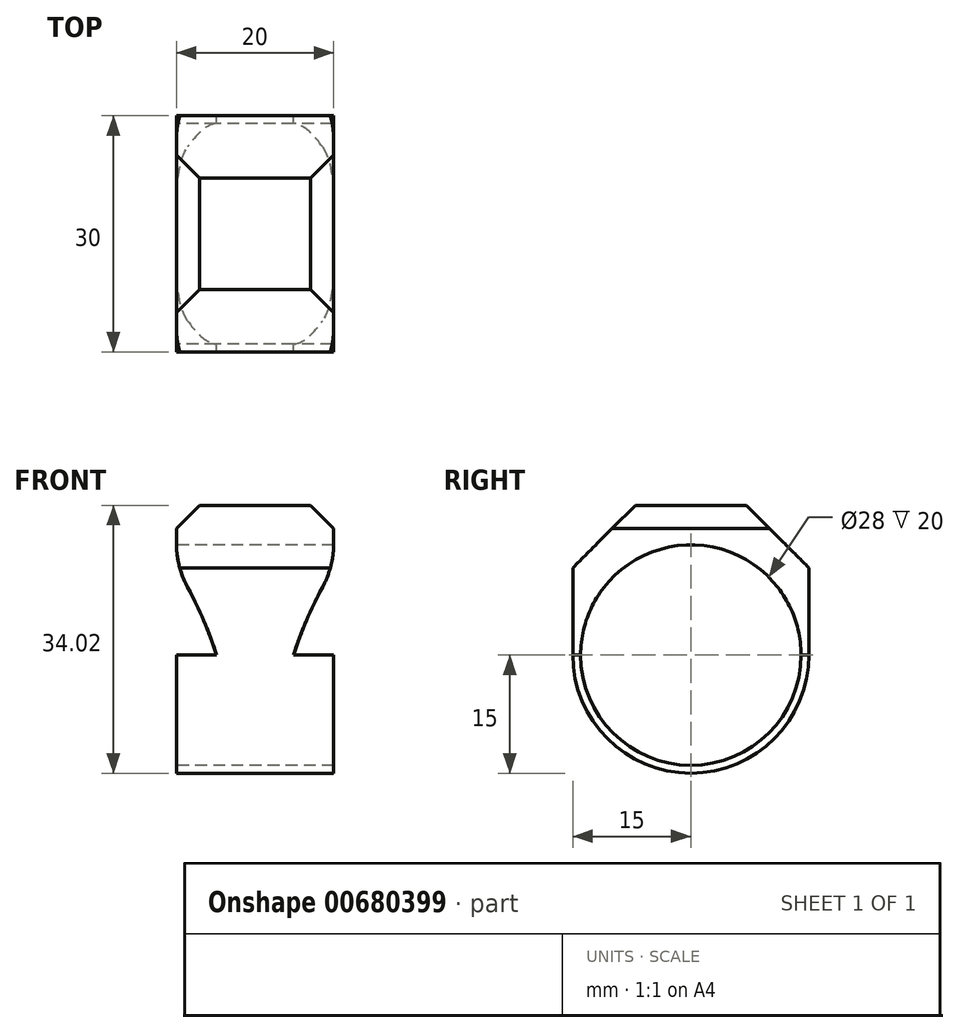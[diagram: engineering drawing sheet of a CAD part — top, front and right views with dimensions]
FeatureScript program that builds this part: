
annotation { "Feature Type Name" : "Feature", "Feature Type Description" : "" }
export const myFeature = defineFeature(function(context is Context, id is Id, definition is map)
    precondition{}
    {
        {
            var Q0;
            Q0=qCreatedBy(makeId("Right.planeOp"),FACE);
            var sketch = newSketch(context, id + "F0", { "sketchPlane" : qUnion([Q0])});
            skCircle(sketch, "E0", {"center": v(0, 0) * mm, "radius": 14 * mm});
            skArc(sketch, "E1", {"start": v(-15, 0) * mm, "mid": v(0, -15) * mm, "end": v(15, 0) * mm});
            skLineSegment(sketch, "E2", {"start": v(15, 0) * mm, "end": v(15, 21.08) * mm});
            skLineSegment(sketch, "E3", {"start": v(-15, 0) * mm, "end": v(-15, 21.08) * mm});
            skLineSegment(sketch, "E4", {"start": v(-15, 21.08) * mm, "end": v(15, 21.08) * mm});
            skSolve(sketch);
        }
        {
            var Q0;
            Q0=qSketchRegion(id+"F0",true);
            extrude(context, id + "F1", {"entities" : qUnion([Q0]), "depth" : 20 * mm, "offsetDistance" : 25 * mm});
        }
        {
            var Q0;
            Q0=makeQuery(id+"F1.opExtrude","SWEPT_EDGE",EDGE,{"disambiguationData":[OSD([sQuery(id+"F0.wireOp",EDGE,"E3"),sQuery(id+"F0.wireOp",EDGE,"E4")])]});
            var Q1;
            Q1=makeQuery(id+"F1.opExtrude","SWEPT_EDGE",EDGE,{"disambiguationData":[OSD([sQuery(id+"F0.wireOp",EDGE,"E2"),sQuery(id+"F0.wireOp",EDGE,"E4")])]});
            chamfer(context, id + "F2", {"entities" : qUnion([Q0, Q1]), "width" : 10 * mm, "tangentPropagation" : true});
        }
        {
            var Q0;
            Q0=makeQuery(id+"F1.opExtrude","SWEPT_FACE",FACE,{"disambiguationData":[OSD([sQuery(id+"F0.wireOp",EDGE,"E2")])]});
            var sketch = newSketch(context, id + "F3", { "sketchPlane" : qUnion([Q0])});
            skLineSegment(sketch, "E5", {"start": v(0, -15) * mm, "end": v(-20, -15) * mm});
            skLineSegment(sketch, "E6", {"start": v(-12.5, -15) * mm, "end": v(-7.5, -15) * mm});
            skArc(sketch, "E7", {"start": v(0, 11.08) * mm, "mid": v(-5.55, -1.44) * mm, "end": v(-7.5, -15) * mm});
            skArc(sketch, "E8", {"start": v(-12.5, -15) * mm, "mid": v(-14.45, -1.44) * mm, "end": v(-20, 11.08) * mm});
            skLineSegment(sketch, "E9", {"start": v(0, 11.08) * mm, "end": v(0, -15) * mm});
            skLineSegment(sketch, "E10", {"start": v(0, -15) * mm, "end": v(-7.5, -15) * mm});
            skLineSegment(sketch, "E11", {"start": v(-20, -15) * mm, "end": v(-20, -15) * mm});
            skLineSegment(sketch, "E12", {"start": v(-20, 11.08) * mm, "end": v(-20, -15) * mm});
            skLineSegment(sketch, "E13.trimOffspring", {"start": v(-12.5, -15) * mm, "end": v(-20, -15) * mm});
            skSolve(sketch);
        }
        {
            var Q0;
            {var subQ0=sQuery(id+"F3.wireOp",EDGE,"E9");var subQ2=sQuery(id+"F0.wireOp",EDGE,"E2");var subQ4=makeQuery(id+"F1.opExtrude","SWEPT_EDGE",EDGE,{"disambiguationData":[OSD([sQuery(id+"F0.wireOp",EDGE,"E1"),subQ2])]});var subQ6=makeQuery(id+"F3.imprint","INTERSECT",VERTEX,{"derivedFrom":[subQ4,subQ0]});Q0=makeQuery(id+"F3.imprint","IMPRINT",FACE,{"disambiguationData":[TD([[makeQuery(id+"F3.imprint","IMPRINT",EDGE,{"disambiguationData":[TD([[subQ6,1.0]])],"derivedFrom":subQ4}),1.0]])]});}
            var Q1;
            {var subQ0=sQuery(id+"F3.wireOp",EDGE,"E12");var subQ2=sQuery(id+"F0.wireOp",EDGE,"E2");var subQ4=makeQuery(id+"F1.opExtrude","SWEPT_EDGE",EDGE,{"disambiguationData":[OSD([sQuery(id+"F0.wireOp",EDGE,"E1"),subQ2])]});var subQ6=makeQuery(id+"F3.imprint","INTERSECT",VERTEX,{"derivedFrom":[subQ4,subQ0]});Q1=makeQuery(id+"F3.imprint","IMPRINT",FACE,{"disambiguationData":[TD([[makeQuery(id+"F3.imprint","IMPRINT",EDGE,{"disambiguationData":[TD([[subQ6,-1.0]])],"derivedFrom":subQ4}),1.0]])]});}
            var Q2;
            {var subQ0=sQuery(id+"F3.wireOp",EDGE,"E13.trimOffspring");Q2=makeQuery(id+"F3.imprint","IMPRINT",FACE,{"disambiguationData":[TD([[makeQuery(id+"F3.imprint","IMPRINT",EDGE,{"derivedFrom":subQ0}),-1.0]])]});}
            var Q3;
            {var subQ0=sQuery(id+"F3.wireOp",EDGE,"E10");Q3=makeQuery(id+"F3.imprint","IMPRINT",FACE,{"disambiguationData":[TD([[makeQuery(id+"F3.imprint","IMPRINT",EDGE,{"derivedFrom":subQ0}),-1.0]])]});}
            extrude(context, id + "F4", {"entities" : qUnion([Q0, Q1, Q2, Q3]), "operationType" : NewBodyOperationType.REMOVE, "oppositeDirection" : true, "depth" : 38.66 * mm, "offsetDistance" : 25 * mm});
        }
        {
            var Q0;
            {var subQ0=sQuery(id+"F0.wireOp",EDGE,"E4");var subQ1=sQuery(id+"F0.wireOp",EDGE,"E2");var subQ3=sQuery(id+"F3.wireOp",EDGE,"E8");Q0=makeQuery(id+"F4.boolean.opBoolean","COPY",EDGE,{"disambiguationData":[TD([makeQuery(id+"F1.opExtrude","SWEPT_FACE",FACE,{"disambiguationData":[OSD([subQ1])]})])],"derivedFrom":makeQuery(id+"F4.opExtrude","SWEPT_EDGE",EDGE,{"disambiguationData":[OSD([subQ1,subQ0,subQ3,sQuery(id+"F3.wireOp",EDGE,"E12")])]})});}
            var Q1;
            {var subQ0=sQuery(id+"F0.wireOp",EDGE,"E4");var subQ1=sQuery(id+"F0.wireOp",EDGE,"E3");var subQ2=sQuery(id+"F0.wireOp",EDGE,"E2");var subQ4=sQuery(id+"F3.wireOp",EDGE,"E8");Q1=makeQuery(id+"F4.boolean.opBoolean","COPY",EDGE,{"disambiguationData":[TD([makeQuery(id+"F1.opExtrude","SWEPT_FACE",FACE,{"disambiguationData":[OSD([subQ1])]})])],"derivedFrom":makeQuery(id+"F4.opExtrude","SWEPT_EDGE",EDGE,{"disambiguationData":[OSD([subQ2,subQ0,subQ4,sQuery(id+"F3.wireOp",EDGE,"E12")])]})});}
            var Q2;
            {var subQ0=sQuery(id+"F0.wireOp",EDGE,"E4");var subQ1=sQuery(id+"F0.wireOp",EDGE,"E3");var subQ2=sQuery(id+"F3.wireOp",EDGE,"E7");var subQ3=sQuery(id+"F0.wireOp",EDGE,"E2");Q2=makeQuery(id+"F4.boolean.opBoolean","COPY",EDGE,{"disambiguationData":[TD([makeQuery(id+"F1.opExtrude","SWEPT_FACE",FACE,{"disambiguationData":[OSD([subQ1])]})])],"derivedFrom":makeQuery(id+"F4.opExtrude","SWEPT_EDGE",EDGE,{"disambiguationData":[OSD([subQ3,subQ0,subQ2,sQuery(id+"F3.wireOp",EDGE,"E9")])]})});}
            var Q3;
            {var subQ0=sQuery(id+"F0.wireOp",EDGE,"E2");var subQ1=sQuery(id+"F0.wireOp",EDGE,"E4");var subQ3=sQuery(id+"F3.wireOp",EDGE,"E7");Q3=makeQuery(id+"F4.boolean.opBoolean","COPY",EDGE,{"disambiguationData":[TD([makeQuery(id+"F1.opExtrude","SWEPT_FACE",FACE,{"disambiguationData":[OSD([subQ0])]})])],"derivedFrom":makeQuery(id+"F4.opExtrude","SWEPT_EDGE",EDGE,{"disambiguationData":[OSD([subQ0,subQ1,subQ3,sQuery(id+"F3.wireOp",EDGE,"E9")])]})});}
            fillet(context, id + "F5", {"entities" : qUnion([Q0, Q1, Q2, Q3]), "radius" : 12 * mm, "tangentPropagation" : true, "allowEdgeOverflow" : false});
        }
        {
            var Q0;
            Q0=makeQuery(id+"F1.opExtrude","CAP_EDGE",EDGE,{"disambiguationData":[OSD([sQuery(id+"F0.wireOp",EDGE,"E4")])],"isStart":true});
            var Q1;
            Q1=makeQuery(id+"F1.opExtrude","CAP_EDGE",EDGE,{"disambiguationData":[OSD([sQuery(id+"F0.wireOp",EDGE,"E4")])],"isStart":false});
            chamfer(context, id + "F6", {"entities" : qUnion([Q0, Q1]), "width" : 5 * mm, "tangentPropagation" : true});
        }
        {
            var Q0;
            Q0=qCreatedBy(makeId("Right.planeOp"),FACE);
            var sketch = newSketch(context, id + "F7", { "sketchPlane" : qUnion([Q0])});
            skLineSegment(sketch, "E14.bottom", {"start": v(23.02, 60.04) * mm, "end": v(-26.86, 60.04) * mm});
            skLineSegment(sketch, "E14.top", {"start": v(23.02, 19.02) * mm, "end": v(-26.86, 19.02) * mm});
            skLineSegment(sketch, "E14.left", {"start": v(23.02, 60.04) * mm, "end": v(23.02, 19.02) * mm});
            skLineSegment(sketch, "E14.right", {"start": v(-26.86, 60.04) * mm, "end": v(-26.86, 19.02) * mm});
            skSolve(sketch);
        }
        {
            var Q0;
            Q0=qSketchRegion(id+"F7",true);
            extrude(context, id + "F8", {"entities" : qUnion([Q0]), "operationType" : NewBodyOperationType.REMOVE, "endBound" : BoundingType.SYMMETRIC, "oppositeDirection" : true, "depth" : 77.2 * mm, "offsetDistance" : 25 * mm});
        }
    });
